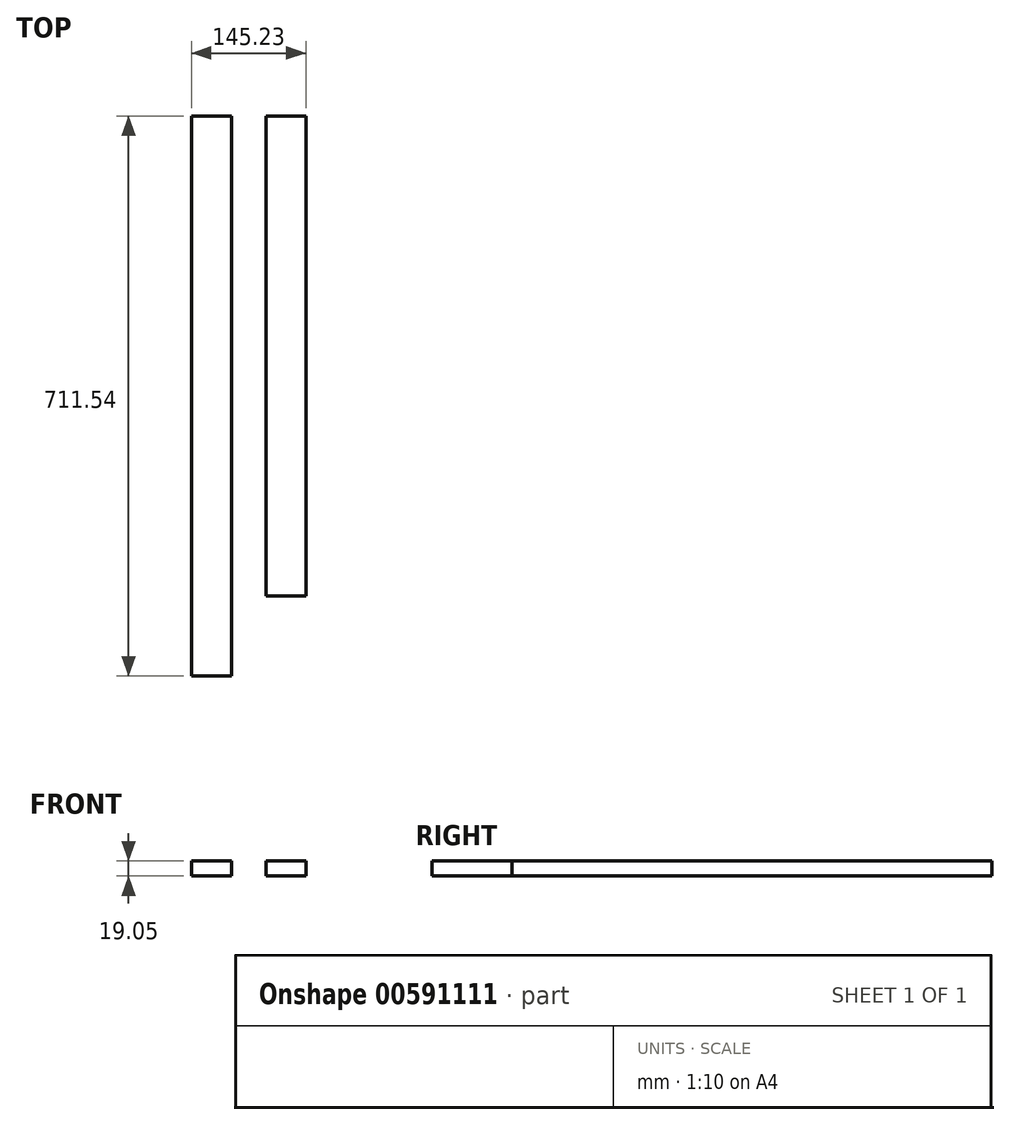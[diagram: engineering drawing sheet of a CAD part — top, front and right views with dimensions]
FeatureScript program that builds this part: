
annotation { "Feature Type Name" : "Feature", "Feature Type Description" : "" }
export const myFeature = defineFeature(function(context is Context, id is Id, definition is map)
    precondition{}
    {
        {
            var Q0;
            Q0=qCreatedBy(makeId("Top.planeOp"),FACE);
            var sketch = newSketch(context, id + "F0", { "sketchPlane" : qUnion([Q0])});
            skLineSegment(sketch, "E0.bottom", {"start": v(0, 22.76) * mm, "end": v(50.8, 22.76) * mm});
            skLineSegment(sketch, "E0.top", {"start": v(0, 632.36) * mm, "end": v(50.8, 632.36) * mm});
            skLineSegment(sketch, "E0.left", {"start": v(0, 22.76) * mm, "end": v(0, 632.36) * mm});
            skLineSegment(sketch, "E0.right", {"start": v(50.8, 22.76) * mm, "end": v(50.8, 632.36) * mm});
            skLineSegment(sketch, "E1.bottom", {"start": v(-94.43, 606.62) * mm, "end": v(-43.63, 606.62) * mm});
            skLineSegment(sketch, "E1.top", {"start": v(-94.43, -53.78) * mm, "end": v(-43.63, -53.78) * mm});
            skLineSegment(sketch, "E1.left", {"start": v(-94.43, 606.62) * mm, "end": v(-94.43, -53.78) * mm});
            skLineSegment(sketch, "E1.right", {"start": v(-43.63, 606.62) * mm, "end": v(-43.63, -53.78) * mm});
            skLineSegment(sketch, "E2", {"start": v(-94.43, 606.62) * mm, "end": v(-94.43, 632.02) * mm});
            skLineSegment(sketch, "E3", {"start": v(-94.43, 632.02) * mm, "end": v(-43.63, 632.02) * mm});
            skLineSegment(sketch, "E4", {"start": v(-43.63, 632.02) * mm, "end": v(-43.63, 606.62) * mm});
            skLineSegment(sketch, "E5", {"start": v(-94.43, -53.78) * mm, "end": v(-94.43, -79.18) * mm});
            skLineSegment(sketch, "E6", {"start": v(-94.43, -79.18) * mm, "end": v(-43.63, -79.18) * mm});
            skLineSegment(sketch, "E7", {"start": v(-43.63, -79.18) * mm, "end": v(-43.63, -53.78) * mm});
            skSolve(sketch);
        }
        {
            var Q0;
            Q0 = qSketchRegion(id + "F0", true);
            extrude(context, id + "F1", {"entities" : qUnion([Q0]), "depth" : 19.05 * mm, "offsetDistance" : 25.4 * mm});
        }
    });
